annotation { "Feature Type Name" : "Feature", "Feature Type Description" : "" }
export const myFeature = defineFeature(function(context is Context, id is Id, definition is map)
    precondition{}
    {
        {
            var Q0;
            Q0=qCreatedBy(makeId("Front.planeOp"),FACE);
            var sketch = newSketch(context, id + "F0", { "sketchPlane" : qUnion([Q0])});
            skText(sketch, "E0", { "text": "Google ", "fontName": "NotoSansCJKtc-Bold.otf"});
            skLineSegment(sketch, "E1.bottom", {"start": v(5.86, 58.25) * mm, "end": v(124.9, 58.25) * mm});
            skLineSegment(sketch, "E1.top", {"start": v(5.86, -38.52) * mm, "end": v(124.9, -38.52) * mm});
            skLineSegment(sketch, "E1.left", {"start": v(5.86, 58.25) * mm, "end": v(5.86, -38.52) * mm});
            skLineSegment(sketch, "E1.right", {"start": v(124.9, 58.25) * mm, "end": v(124.9, -38.52) * mm});
            skLineSegment(sketch, "E2.bottom", {"start": v(0, 64.67) * mm, "end": v(130.03, 64.67) * mm});
            skLineSegment(sketch, "E2.top", {"start": v(0, -45.8) * mm, "end": v(130.03, -45.8) * mm});
            skLineSegment(sketch, "E2.left", {"start": v(0, 64.67) * mm, "end": v(0, -45.8) * mm});
            skLineSegment(sketch, "E2.right", {"start": v(130.03, 64.67) * mm, "end": v(130.03, -45.8) * mm});
            skLineSegment(sketch, "E3", {"start": v(-31.3, 35.82) * mm, "end": v(-31.3, 32.7) * mm});
            skLineSegment(sketch, "E4", {"start": v(-33.53, 35.16) * mm, "end": v(-33.53, 30.4) * mm});
            skLineSegment(sketch, "E5", {"start": v(-33.53, 30.4) * mm, "end": v(-29.58, 30.4) * mm});
            skLineSegment(sketch, "E6", {"start": v(-29.58, 30.4) * mm, "end": v(-27.53, 28.91) * mm});
            skLineSegment(sketch, "E7", {"start": v(-27.53, 28.91) * mm, "end": v(-27.53, 21.1) * mm});
            skLineSegment(sketch, "E8", {"start": v(-27.53, 21.1) * mm, "end": v(-29.42, 21.1) * mm});
            skLineSegment(sketch, "E9", {"start": v(-29.42, 21.1) * mm, "end": v(-31.15, 19.94) * mm});
            skLineSegment(sketch, "E10", {"start": v(-31.15, 19.94) * mm, "end": v(-25.47, 19.94) * mm});
            skLineSegment(sketch, "E11", {"start": v(-25.47, 19.94) * mm, "end": v(-25.47, 25.54) * mm});
            skLineSegment(sketch, "E12", {"start": v(-25.47, 25.54) * mm, "end": v(-22.5, 25.54) * mm});
            skLineSegment(sketch, "E13", {"start": v(-22.5, 25.54) * mm, "end": v(-22.5, 19.94) * mm});
            skLineSegment(sketch, "E14", {"start": v(-22.5, 19.94) * mm, "end": v(-18.64, 19.94) * mm});
            skLineSegment(sketch, "E15", {"start": v(-18.64, 19.94) * mm, "end": v(-19.4, 21.1) * mm});
            skLineSegment(sketch, "E16", {"start": v(-19.4, 21.1) * mm, "end": v(-20.86, 21.1) * mm});
            skLineSegment(sketch, "E17", {"start": v(-20.86, 21.1) * mm, "end": v(-20.86, 25.54) * mm});
            skLineSegment(sketch, "E18", {"start": v(-20.86, 25.54) * mm, "end": v(-20.86, 28.5) * mm});
            skLineSegment(sketch, "E19", {"start": v(-20.86, 28.5) * mm, "end": v(-18.9, 29.8) * mm});
            skLineSegment(sketch, "E20", {"start": v(-16.34, 29.8) * mm, "end": v(-18.9, 29.8) * mm});
            skLineSegment(sketch, "E21", {"start": v(-16.34, 29.8) * mm, "end": v(-16.34, 35) * mm});
            skLineSegment(sketch, "E22", {"start": v(-18.56, 35.82) * mm, "end": v(-18.56, 32.61) * mm});
            skLineSegment(sketch, "E23", {"start": v(-18.56, 32.61) * mm, "end": v(-21.27, 32.61) * mm});
            skLineSegment(sketch, "E24", {"start": v(-31.3, 32.7) * mm, "end": v(-26.84, 32.7) * mm});
            skLineSegment(sketch, "E25", {"start": v(-26.84, 32.7) * mm, "end": v(-26.84, 34.08) * mm});
            skLineSegment(sketch, "E26", {"start": v(-21.27, 32.61) * mm, "end": v(-21.27, 34.08) * mm});
            skArc(sketch, "E27", {"start": v(-24.99, 36.16) * mm, "mid": v(-26.31, 35.47) * mm, "end": v(-26.84, 34.08) * mm});
            skArc(sketch, "E28", {"start": v(-21.27, 34.08) * mm, "mid": v(-22.7, 35.9) * mm, "end": v(-24.99, 36.16) * mm});
            skArc(sketch, "E29", {"start": v(-26.84, 34.08) * mm, "mid": v(-26.64, 32.2) * mm, "end": v(-24.99, 31.3) * mm});
            skArc(sketch, "E30", {"start": v(-24.99, 31.3) * mm, "mid": v(-22.43, 31.76) * mm, "end": v(-21.27, 34.08) * mm});
            skLineSegment(sketch, "E31.bottom", {"start": v(150.76, 67.7) * mm, "end": v(295.17, 67.7) * mm});
            skLineSegment(sketch, "E31.top", {"start": v(150.76, -35.75) * mm, "end": v(295.17, -35.75) * mm});
            skLineSegment(sketch, "E31.left", {"start": v(150.76, 67.7) * mm, "end": v(150.76, -35.75) * mm});
            skLineSegment(sketch, "E31.right", {"start": v(295.17, 67.7) * mm, "end": v(295.17, -35.75) * mm});
            skPoint(sketch, "E32.oppositeSnap0", {"position": v(222.96, 67.7) * mm});
            skLineSegment(sketch, "E32.bottom", {"start": v(222.96, 67.7) * mm, "end": v(222.96, 67.7) * mm});
            skLineSegment(sketch, "E32.top", {"start": v(222.96, 106.62) * mm, "end": v(222.96, 106.62) * mm});
            skLineSegment(sketch, "E32.left", {"start": v(222.96, 67.7) * mm, "end": v(222.96, 106.62) * mm});
            skLineSegment(sketch, "E32.right", {"start": v(222.96, 67.7) * mm, "end": v(222.96, 106.62) * mm});
            skLineSegment(sketch, "E33", {"start": v(150.76, 67.7) * mm, "end": v(222.96, 106.62) * mm});
            skLineSegment(sketch, "E34", {"start": v(295.17, 67.7) * mm, "end": v(222.96, 106.62) * mm});
            const initialGuessF0  = {"E0": [-0.06541, -0.02444, 1, 0, 0.07026]};
            skSetInitialGuess(sketch, initialGuessF0);
            skSolve(sketch);
        }
        {
            var Q0;
            Q0=makeQuery(id+"F0.imprint","IMPRINT",FACE,{"disambiguationData":[TD([[makeQuery(id+"F0.imprint","IMPRINT",EDGE,{"derivedFrom":sQuery(id+"F0.wireOp",EDGE,"E0.sketch_text.stroke-0")}),1.0]])]});
            var Q1;
            Q1=makeQuery(id+"F0.imprint","IMPRINT",FACE,{"disambiguationData":[TD([[makeQuery(id+"F0.imprint","IMPRINT",EDGE,{"derivedFrom":sQuery(id+"F0.wireOp",EDGE,"E0.sketch_text.stroke-14")}),1.0]])]});
            var Q2;
            Q2=makeQuery(id+"F0.imprint","IMPRINT",FACE,{"disambiguationData":[TD([[makeQuery(id+"F0.imprint","IMPRINT",EDGE,{"derivedFrom":sQuery(id+"F0.wireOp",EDGE,"E0.sketch_text.stroke-22")}),1.0]])]});
            var Q3;
            Q3=makeQuery(id+"F0.imprint","IMPRINT",FACE,{"disambiguationData":[TD([[makeQuery(id+"F0.imprint","IMPRINT",EDGE,{"derivedFrom":sQuery(id+"F0.wireOp",EDGE,"E0.sketch_text.stroke-30")}),1.0]])]});
            var Q4;
            Q4=makeQuery(id+"F0.imprint","IMPRINT",FACE,{"disambiguationData":[TD([[makeQuery(id+"F0.imprint","IMPRINT",EDGE,{"derivedFrom":sQuery(id+"F0.wireOp",EDGE,"E0.sketch_text.stroke-60")}),1.0]])]});
            var Q5;
            Q5=makeQuery(id+"F0.imprint","IMPRINT",FACE,{"disambiguationData":[TD([[makeQuery(id+"F0.imprint","IMPRINT",EDGE,{"derivedFrom":sQuery(id+"F0.wireOp",EDGE,"E0.sketch_text.stroke-68")}),1.0]])]});
            extrude(context, id + "F1", {"entities" : qUnion([Q0, Q1, Q2, Q3, Q4, Q5]), "depth" : 25 * mm, "offsetDistance" : 25 * mm});
        }
        {
            var Q0;
            Q0=makeQuery(id+"F0.imprint","IMPRINT",FACE,{"disambiguationData":[TD([[makeQuery(id+"F0.imprint","IMPRINT",EDGE,{"derivedFrom":sQuery(id+"F0.wireOp",EDGE,"E1.bottom")}),1.0]])]});
            extrude(context, id + "F2", {"entities" : qUnion([Q0]), "depth" : 2.5 * mm, "offsetDistance" : 25 * mm});
        }
        {
            var Q0;
            Q0=makeQuery(id+"F0.imprint","IMPRINT",FACE,{"disambiguationData":[TD([[makeQuery(id+"F0.imprint","IMPRINT",EDGE,{"derivedFrom":sQuery(id+"F0.wireOp",EDGE,"E0.sketch_text.stroke-14")}),-1.0]])]});
            extrude(context, id + "F3", {"entities" : qUnion([Q0]), "depth" : 1 * mm, "offsetDistance" : 25 * mm});
        }
        {
            var Q0;
            Q0=makeQuery(id+"F3.opExtrude","CAP_FACE",FACE,{"disambiguationData":[OSD([sQuery(id+"F0.wireOp",EDGE,"E0.sketch_text.stroke-14"),sQuery(id+"F0.wireOp",EDGE,"E0.sketch_text.stroke-15"),sQuery(id+"F0.wireOp",EDGE,"E0.sketch_text.stroke-16"),sQuery(id+"F0.wireOp",EDGE,"E0.sketch_text.stroke-17"),sQuery(id+"F0.wireOp",EDGE,"E0.sketch_text.stroke-22"),sQuery(id+"F0.wireOp",EDGE,"E0.sketch_text.stroke-23"),sQuery(id+"F0.wireOp",EDGE,"E0.sketch_text.stroke-24"),sQuery(id+"F0.wireOp",EDGE,"E0.sketch_text.stroke-25"),sQuery(id+"F0.wireOp",EDGE,"E1.bottom"),sQuery(id+"F0.wireOp",EDGE,"E1.top"),sQuery(id+"F0.wireOp",EDGE,"E1.left"),sQuery(id+"F0.wireOp",EDGE,"E1.right")])],"isStart":false});
            var sketch = newSketch(context, id + "F4", { "sketchPlane" : qUnion([Q0])});
            skText(sketch, "E35", { "text": "Edukasja", "fontName": "OpenSans-Bold.ttf"});
            skText(sketch, "E36", { "text": "Ausbildung", "fontName": "OpenSans-Bold.ttf"});
            skText(sketch, "E37", { "text": "Education", "fontName": "OpenSans-Bold.ttf"});
            skText(sketch, "E38", { "text": "Svietnas", "fontName": "OpenSans-Regular.ttf"});
            skText(sketch, "E39", { "text": "Educasim", "fontName": "OpenSans-Regular.ttf"});
            const initialGuessF4  = {"E35": [0.0131, 0.05001, 1, 0, 0.0053], "E36": [0.06463, 0.04333, 1, 0, 0.00669], "E37": [0.03588, 0.0381, 0.96593, -0.25882, 0.00613], "E38": [0.07327, -0.03612, 1, 0, 0.00935], "E39": [0.0169, -0.03634, 1, 0, 0.00632]};
            skSetInitialGuess(sketch, initialGuessF4);
            skSolve(sketch);
        }
        {
            var Q0;
            Q0 = qSketchRegion(id + "F4", true);
            extrude(context, id + "F5", {"entities" : qUnion([Q0]), "operationType" : NewBodyOperationType.ADD, "depth" : 1.1 * mm, "offsetDistance" : 25 * mm});
        }
        {
            var Q0;
            {var subQ12=sQuery(id+"F0.wireOp",EDGE,"E5");Q0=makeQuery(id+"F0.imprint","IMPRINT",FACE,{"disambiguationData":[TD([[makeQuery(id+"F0.imprint","IMPRINT",EDGE,{"derivedFrom":subQ12}),1.0]])]});}
            var Q1;
            {var subQ0=sQuery(id+"F0.wireOp",EDGE,"E25");Q1=makeQuery(id+"F0.imprint","IMPRINT",FACE,{"disambiguationData":[TD([[makeQuery(id+"F0.imprint","IMPRINT",EDGE,{"derivedFrom":subQ0}),-1.0]])]});}
            extrude(context, id + "F6", {"entities" : qUnion([Q0, Q1]), "operationType" : NewBodyOperationType.ADD, "depth" : 15 * mm, "offsetDistance" : 25 * mm});
        }
        {
            var Q0;
            {var subQ2=sQuery(id+"F0.wireOp",EDGE,"E32.right");Q0=makeQuery(id+"F0.imprint","IMPRINT",FACE,{"disambiguationData":[TD([[makeQuery(id+"F0.imprint","IMPRINT",EDGE,{"derivedFrom":subQ2}),1.0]])]});}
            var Q1;
            {var subQ2=sQuery(id+"F0.wireOp",EDGE,"E32.right");Q1=makeQuery(id+"F0.imprint","IMPRINT",FACE,{"disambiguationData":[TD([[makeQuery(id+"F0.imprint","IMPRINT",EDGE,{"derivedFrom":subQ2}),-1.0]])]});}
            var Q2;
            {var subQ10=sQuery(id+"F0.wireOp",EDGE,"E0.sketch_text.stroke-31");Q2=makeQuery(id+"F0.imprint","IMPRINT",FACE,{"disambiguationData":[TD([[makeQuery(id+"F0.imprint","IMPRINT",EDGE,{"derivedFrom":subQ10}),-1.0]])]});}
            extrude(context, id + "F7", {"entities" : qUnion([Q0, Q1, Q2]), "depth" : 2.5 * mm, "offsetDistance" : 25 * mm});
        }
        {
            var Q0;
            {var subQ8=sQuery(id+"F0.wireOp",EDGE,"E0.sketch_text.stroke-34");Q0=makeQuery(id+"F0.imprint","IMPRINT",FACE,{"disambiguationData":[TD([[makeQuery(id+"F0.imprint","IMPRINT",EDGE,{"derivedFrom":subQ8}),1.0]])]});}
            var Q1;
            {var subQ12=sQuery(id+"F0.wireOp",EDGE,"E0.sketch_text.stroke-36");Q1=makeQuery(id+"F0.imprint","IMPRINT",FACE,{"disambiguationData":[TD([[makeQuery(id+"F0.imprint","IMPRINT",EDGE,{"derivedFrom":subQ12}),1.0]])]});}
            extrude(context, id + "F8", {"entities" : qUnion([Q0, Q1]), "depth" : 25 * mm, "offsetDistance" : 25 * mm});
        }
        {
            var Q0;
            Q0=makeQuery(id+"F7.opExtrude","CAP_FACE",FACE,{"disambiguationData":[OSD([sQuery(id+"F0.wireOp",EDGE,"E0.sketch_text.stroke-30"),sQuery(id+"F0.wireOp",EDGE,"E0.sketch_text.stroke-31"),sQuery(id+"F0.wireOp",EDGE,"E0.sketch_text.stroke-32"),sQuery(id+"F0.wireOp",EDGE,"E0.sketch_text.stroke-33"),sQuery(id+"F0.wireOp",EDGE,"E0.sketch_text.stroke-35"),sQuery(id+"F0.wireOp",EDGE,"E0.sketch_text.stroke-36"),sQuery(id+"F0.wireOp",EDGE,"E0.sketch_text.stroke-37"),sQuery(id+"F0.wireOp",EDGE,"E0.sketch_text.stroke-38"),sQuery(id+"F0.wireOp",EDGE,"E0.sketch_text.stroke-39"),sQuery(id+"F0.wireOp",EDGE,"E0.sketch_text.stroke-40"),sQuery(id+"F0.wireOp",EDGE,"E0.sketch_text.stroke-41"),sQuery(id+"F0.wireOp",EDGE,"E0.sketch_text.stroke-42"),sQuery(id+"F0.wireOp",EDGE,"E0.sketch_text.stroke-60"),sQuery(id+"F0.wireOp",EDGE,"E0.sketch_text.stroke-61"),sQuery(id+"F0.wireOp",EDGE,"E0.sketch_text.stroke-62"),sQuery(id+"F0.wireOp",EDGE,"E0.sketch_text.stroke-63"),sQuery(id+"F0.wireOp",EDGE,"E0.sketch_text.stroke-64"),sQuery(id+"F0.wireOp",EDGE,"E0.sketch_text.stroke-65"),sQuery(id+"F0.wireOp",EDGE,"E0.sketch_text.stroke-66"),sQuery(id+"F0.wireOp",EDGE,"E0.sketch_text.stroke-67"),sQuery(id+"F0.wireOp",EDGE,"E0.sketch_text.stroke-68"),sQuery(id+"F0.wireOp",EDGE,"E0.sketch_text.stroke-69"),sQuery(id+"F0.wireOp",EDGE,"E0.sketch_text.stroke-70"),sQuery(id+"F0.wireOp",EDGE,"E0.sketch_text.stroke-71"),sQuery(id+"F0.wireOp",EDGE,"E0.sketch_text.stroke-72"),sQuery(id+"F0.wireOp",EDGE,"E0.sketch_text.stroke-73"),sQuery(id+"F0.wireOp",EDGE,"E0.sketch_text.stroke-74"),sQuery(id+"F0.wireOp",EDGE,"E0.sketch_text.stroke-75"),sQuery(id+"F0.wireOp",EDGE,"E0.sketch_text.stroke-76"),sQuery(id+"F0.wireOp",EDGE,"E31.top"),sQuery(id+"F0.wireOp",EDGE,"E31.left"),sQuery(id+"F0.wireOp",EDGE,"E31.right"),sQuery(id+"F0.wireOp",EDGE,"E33"),sQuery(id+"F0.wireOp",EDGE,"E34")])],"isStart":false});
            var sketch = newSketch(context, id + "F9", { "sketchPlane" : qUnion([Q0])});
            skPoint(sketch, "E40.firstSnap0", {"position": v(186.86, 87.16) * mm});
            skText(sketch, "E41", { "text": "Sport Facility\n", "fontName": "OpenSans-Regular.ttf"});
            const initialGuessF9  = {"E41": [0.18162, 0.0634, 1, 0, 0.01163]};
            skSetInitialGuess(sketch, initialGuessF9);
            skSolve(sketch);
        }
        {
            var Q0;
            Q0=makeQuery(id+"F9.imprint","IMPRINT",FACE,{"disambiguationData":[TD([[makeQuery(id+"F9.imprint","IMPRINT",EDGE,{"derivedFrom":sQuery(id+"F9.wireOp",EDGE,"E41.sketch_text.stroke-0")}),-1.0]])]});
            var Q1;
            Q1=makeQuery(id+"F9.imprint","IMPRINT",FACE,{"disambiguationData":[TD([[makeQuery(id+"F9.imprint","IMPRINT",EDGE,{"derivedFrom":sQuery(id+"F9.wireOp",EDGE,"E41.sketch_text.stroke-25")}),-1.0]])]});
            var Q2;
            Q2=makeQuery(id+"F9.imprint","IMPRINT",FACE,{"disambiguationData":[TD([[makeQuery(id+"F9.imprint","IMPRINT",EDGE,{"derivedFrom":sQuery(id+"F9.wireOp",EDGE,"E41.sketch_text.stroke-50")}),-1.0]])]});
            var Q3;
            Q3=makeQuery(id+"F9.imprint","IMPRINT",FACE,{"disambiguationData":[TD([[makeQuery(id+"F9.imprint","IMPRINT",EDGE,{"derivedFrom":sQuery(id+"F9.wireOp",EDGE,"E41.sketch_text.stroke-67")}),-1.0]])]});
            var Q4;
            Q4=makeQuery(id+"F9.imprint","IMPRINT",FACE,{"disambiguationData":[TD([[makeQuery(id+"F9.imprint","IMPRINT",EDGE,{"derivedFrom":sQuery(id+"F9.wireOp",EDGE,"E41.sketch_text.stroke-80")}),-1.0]])]});
            var Q5;
            Q5=makeQuery(id+"F9.imprint","IMPRINT",FACE,{"disambiguationData":[TD([[makeQuery(id+"F9.imprint","IMPRINT",EDGE,{"derivedFrom":sQuery(id+"F9.wireOp",EDGE,"E41.sketch_text.stroke-99")}),-1.0]])]});
            var Q6;
            Q6=makeQuery(id+"F9.imprint","IMPRINT",FACE,{"disambiguationData":[TD([[makeQuery(id+"F9.imprint","IMPRINT",EDGE,{"derivedFrom":sQuery(id+"F9.wireOp",EDGE,"E41.sketch_text.stroke-109")}),-1.0]])]});
            var Q7;
            Q7=makeQuery(id+"F9.imprint","IMPRINT",FACE,{"disambiguationData":[TD([[makeQuery(id+"F9.imprint","IMPRINT",EDGE,{"derivedFrom":sQuery(id+"F9.wireOp",EDGE,"E41.sketch_text.stroke-136")}),-1.0]])]});
            var Q8;
            Q8=makeQuery(id+"F9.imprint","IMPRINT",FACE,{"disambiguationData":[TD([[makeQuery(id+"F9.imprint","IMPRINT",EDGE,{"derivedFrom":sQuery(id+"F9.wireOp",EDGE,"E41.sketch_text.stroke-151")}),-1.0]])]});
            var Q9;
            Q9=makeQuery(id+"F9.imprint","IMPRINT",FACE,{"disambiguationData":[TD([[makeQuery(id+"F9.imprint","IMPRINT",EDGE,{"derivedFrom":sQuery(id+"F9.wireOp",EDGE,"E41.sketch_text.stroke-163")}),-1.0]])]});
            var Q10;
            Q10=makeQuery(id+"F9.imprint","IMPRINT",FACE,{"disambiguationData":[TD([[makeQuery(id+"F9.imprint","IMPRINT",EDGE,{"derivedFrom":sQuery(id+"F9.wireOp",EDGE,"E41.sketch_text.stroke-167")}),-1.0]])]});
            var Q11;
            Q11=makeQuery(id+"F9.imprint","IMPRINT",FACE,{"disambiguationData":[TD([[makeQuery(id+"F9.imprint","IMPRINT",EDGE,{"derivedFrom":sQuery(id+"F9.wireOp",EDGE,"E41.sketch_text.stroke-171")}),-1.0]])]});
            var Q12;
            Q12=makeQuery(id+"F9.imprint","IMPRINT",FACE,{"disambiguationData":[TD([[makeQuery(id+"F9.imprint","IMPRINT",EDGE,{"derivedFrom":sQuery(id+"F9.wireOp",EDGE,"E41.sketch_text.stroke-155")}),-1.0]])]});
            var Q13;
            Q13=makeQuery(id+"F9.imprint","IMPRINT",FACE,{"disambiguationData":[TD([[makeQuery(id+"F9.imprint","IMPRINT",EDGE,{"derivedFrom":sQuery(id+"F9.wireOp",EDGE,"E41.sketch_text.stroke-179")}),-1.0]])]});
            var Q14;
            Q14=makeQuery(id+"F9.imprint","IMPRINT",FACE,{"disambiguationData":[TD([[makeQuery(id+"F9.imprint","IMPRINT",EDGE,{"derivedFrom":sQuery(id+"F9.wireOp",EDGE,"E41.sketch_text.stroke-198")}),-1.0]])]});
            extrude(context, id + "F10", {"entities" : qUnion([Q0, Q1, Q2, Q3, Q4, Q5, Q6, Q7, Q8, Q9, Q10, Q11, Q12, Q13, Q14]), "operationType" : NewBodyOperationType.ADD, "depth" : 1 * mm, "offsetDistance" : 25 * mm});
        }
        {
            var Q0;
            {var subQ0=sQuery(id+"F0.wireOp",EDGE,"E34");var subQ1=sQuery(id+"F0.wireOp",EDGE,"E33");var subQ2=sQuery(id+"F0.wireOp",EDGE,"E31.right");var subQ3=sQuery(id+"F0.wireOp",EDGE,"E31.left");var subQ4=sQuery(id+"F0.wireOp",EDGE,"E0.sketch_text.stroke-33");var subQ5=sQuery(id+"F0.wireOp",EDGE,"E0.sketch_text.stroke-35");var subQ6=sQuery(id+"F0.wireOp",EDGE,"E0.sketch_text.stroke-42");var subQ7=sQuery(id+"F0.wireOp",EDGE,"E31.top");var subQ8=sQuery(id+"F0.wireOp",EDGE,"E0.sketch_text.stroke-76");var subQ9=sQuery(id+"F0.wireOp",EDGE,"E0.sketch_text.stroke-75");var subQ10=sQuery(id+"F0.wireOp",EDGE,"E0.sketch_text.stroke-74");var subQ11=sQuery(id+"F0.wireOp",EDGE,"E0.sketch_text.stroke-73");var subQ12=sQuery(id+"F0.wireOp",EDGE,"E0.sketch_text.stroke-72");var subQ13=sQuery(id+"F0.wireOp",EDGE,"E0.sketch_text.stroke-71");var subQ14=sQuery(id+"F0.wireOp",EDGE,"E0.sketch_text.stroke-70");var subQ15=sQuery(id+"F0.wireOp",EDGE,"E0.sketch_text.stroke-69");var subQ16=sQuery(id+"F0.wireOp",EDGE,"E0.sketch_text.stroke-68");var subQ17=sQuery(id+"F0.wireOp",EDGE,"E0.sketch_text.stroke-67");var subQ18=sQuery(id+"F0.wireOp",EDGE,"E0.sketch_text.stroke-66");var subQ19=sQuery(id+"F0.wireOp",EDGE,"E0.sketch_text.stroke-63");var subQ20=sQuery(id+"F0.wireOp",EDGE,"E0.sketch_text.stroke-62");var subQ21=sQuery(id+"F0.wireOp",EDGE,"E0.sketch_text.stroke-61");var subQ22=sQuery(id+"F0.wireOp",EDGE,"E0.sketch_text.stroke-39");var subQ23=sQuery(id+"F0.wireOp",EDGE,"E0.sketch_text.stroke-41");var subQ24=sQuery(id+"F0.wireOp",EDGE,"E0.sketch_text.stroke-38");var subQ25=sQuery(id+"F0.wireOp",EDGE,"E0.sketch_text.stroke-40");var subQ26=sQuery(id+"F0.wireOp",EDGE,"E0.sketch_text.stroke-37");var subQ27=sQuery(id+"F0.wireOp",EDGE,"E0.sketch_text.stroke-36");var subQ28=sQuery(id+"F0.wireOp",EDGE,"E0.sketch_text.stroke-30");var subQ29=sQuery(id+"F0.wireOp",EDGE,"E0.sketch_text.stroke-31");var subQ30=sQuery(id+"F0.wireOp",EDGE,"E0.sketch_text.stroke-32");var subQ31=sQuery(id+"F0.wireOp",EDGE,"E0.sketch_text.stroke-60");var subQ32=sQuery(id+"F0.wireOp",EDGE,"E0.sketch_text.stroke-64");var subQ33=sQuery(id+"F0.wireOp",EDGE,"E0.sketch_text.stroke-65");Q0=makeQuery(id+"F10.boolean.opBoolean","SPLIT",FACE,{"disambiguationData":[TD([makeQuery(id+"F7.opExtrude","SWEPT_FACE",FACE,{"disambiguationData":[OSD([subQ28])]})])],"derivedFrom":makeQuery(id+"F7.opExtrude","CAP_FACE",FACE,{"disambiguationData":[OSD([subQ28,subQ29,subQ30,subQ4,subQ5,subQ27,subQ26,subQ24,subQ22,subQ25,subQ23,subQ6,subQ31,subQ21,subQ20,subQ19,subQ32,subQ33,subQ18,subQ17,subQ16,subQ15,subQ14,subQ13,subQ12,subQ11,subQ10,subQ9,subQ8,subQ7,subQ3,subQ2,subQ1,subQ0])],"isStart":false})});}
            var sketch = newSketch(context, id + "F11", { "sketchPlane" : qUnion([Q0])});
            skArc(sketch, "E42", {"start": v(265.82, 51.24) * mm, "mid": v(256.9, 55.6) * mm, "end": v(248.07, 51.03) * mm});
            skArc(sketch, "E43", {"start": v(248.07, 51.03) * mm, "mid": v(256.99, 47.4) * mm, "end": v(265.82, 51.24) * mm});
            skCircle(sketch, "E44", {"center": v(169.8, 54.42) * mm, "radius": 7.64 * mm});
            skLineSegment(sketch, "E45", {"start": v(169.8, 54.42) * mm, "end": v(177.43, 54.42) * mm});
            skLineSegment(sketch, "E46", {"start": v(169.8, 54.42) * mm, "end": v(169.8, 62.06) * mm});
            skLineSegment(sketch, "E47", {"start": v(169.8, 54.42) * mm, "end": v(169.8, 46.79) * mm});
            skLineSegment(sketch, "E48", {"start": v(169.8, 54.42) * mm, "end": v(162.16, 54.42) * mm});
            skLineSegment(sketch, "E49", {"start": v(165.98, 54.42) * mm, "end": v(165.98, 50.79) * mm});
            skLineSegment(sketch, "E50", {"start": v(165.98, 50.79) * mm, "end": v(169.8, 50.79) * mm});
            skLineSegment(sketch, "E51", {"start": v(169.8, 50.79) * mm, "end": v(173.9, 50.79) * mm});
            skLineSegment(sketch, "E52", {"start": v(173.9, 50.79) * mm, "end": v(173.9, 54.42) * mm});
            skLineSegment(sketch, "E53", {"start": v(173.9, 54.42) * mm, "end": v(173.9, 57.38) * mm});
            skLineSegment(sketch, "E54", {"start": v(173.9, 57.38) * mm, "end": v(169.8, 57.38) * mm});
            skLineSegment(sketch, "E55", {"start": v(169.8, 57.38) * mm, "end": v(167.01, 57.38) * mm});
            skLineSegment(sketch, "E56", {"start": v(165.98, 54.42) * mm, "end": v(165.98, 57.38) * mm});
            skLineSegment(sketch, "E57", {"start": v(173.9, 57.38) * mm, "end": v(173.9, 60.86) * mm});
            skLineSegment(sketch, "E58", {"start": v(173.9, 60.86) * mm, "end": v(173.9, 47.98) * mm});
            skLineSegment(sketch, "E59", {"start": v(173.9, 47.98) * mm, "end": v(165.98, 47.98) * mm});
            skLineSegment(sketch, "E60", {"start": v(165.98, 47.98) * mm, "end": v(165.98, 61.03) * mm});
            skLineSegment(sketch, "E61", {"start": v(165.98, 57.38) * mm, "end": v(167.01, 57.38) * mm});
            skLineSegment(sketch, "E62", {"start": v(173.9, 57.38) * mm, "end": v(176.83, 57.38) * mm});
            skLineSegment(sketch, "E63", {"start": v(173.9, 50.79) * mm, "end": v(176.51, 50.79) * mm});
            skLineSegment(sketch, "E64", {"start": v(165.98, 50.79) * mm, "end": v(163.08, 50.79) * mm});
            skLineSegment(sketch, "E65", {"start": v(165.98, 57.38) * mm, "end": v(162.76, 57.38) * mm});
            skCircle(sketch, "E66", {"center": v(222.78, 43.5) * mm, "radius": 4.45 * mm});
            skLineSegment(sketch, "E67.bottom", {"start": v(273.54, 18.71) * mm, "end": v(291.44, 18.71) * mm});
            skLineSegment(sketch, "E67.top", {"start": v(273.54, 5.89) * mm, "end": v(291.44, 5.89) * mm});
            skLineSegment(sketch, "E67.left", {"start": v(273.54, 18.71) * mm, "end": v(273.54, 5.89) * mm});
            skLineSegment(sketch, "E67.right", {"start": v(291.44, 18.71) * mm, "end": v(291.44, 5.89) * mm});
            skLineSegment(sketch, "E68", {"start": v(276.73, 5.89) * mm, "end": v(276.73, 12.64) * mm});
            skLineSegment(sketch, "E69", {"start": v(276.73, 12.64) * mm, "end": v(287.77, 12.64) * mm});
            skLineSegment(sketch, "E70", {"start": v(287.77, 12.64) * mm, "end": v(287.77, 5.89) * mm});
            skArc(sketch, "E71", {"start": v(276.73, 5.89) * mm, "mid": v(282.25, -0.98) * mm, "end": v(287.77, 5.89) * mm});
            skLineSegment(sketch, "E72", {"start": v(270.62, 31.67) * mm, "end": v(272.04, 30.25) * mm});
            skLineSegment(sketch, "E73", {"start": v(272.04, 30.25) * mm, "end": v(277.93, 34.72) * mm});
            skLineSegment(sketch, "E74", {"start": v(270.62, 31.67) * mm, "end": v(276.23, 35.93) * mm});
            skArc(sketch, "E75", {"start": v(279.66, 45.18) * mm, "mid": v(276.45, 41.1) * mm, "end": v(276.23, 35.93) * mm});
            skArc(sketch, "E76", {"start": v(285.95, 45.18) * mm, "mid": v(282.8, 46) * mm, "end": v(279.66, 45.18) * mm});
            skArc(sketch, "E77", {"start": v(287.88, 39.08) * mm, "mid": v(287.82, 42.42) * mm, "end": v(285.95, 45.18) * mm});
            skArc(sketch, "E78", {"start": v(277.93, 34.72) * mm, "mid": v(283.88, 34.67) * mm, "end": v(287.88, 39.08) * mm});
            skCircle(sketch, "E79", {"center": v(287.07, 32.08) * mm, "radius": 1.28 * mm});
            skLineSegment(sketch, "E80", {"start": v(274.33, -28.86) * mm, "end": v(279.32, -28.86) * mm});
            skLineSegment(sketch, "E81", {"start": v(274.33, -28.86) * mm, "end": v(276.63, -27.41) * mm});
            skLineSegment(sketch, "E82", {"start": v(276.63, -27.41) * mm, "end": v(278.07, -27.41) * mm});
            skLineSegment(sketch, "E83", {"start": v(278.07, -27.41) * mm, "end": v(278.07, -18.67) * mm});
            skLineSegment(sketch, "E84", {"start": v(279.32, -28.86) * mm, "end": v(279.32, -21.65) * mm});
            skLineSegment(sketch, "E85", {"start": v(279.32, -21.65) * mm, "end": v(281.82, -21.65) * mm});
            skLineSegment(sketch, "E86", {"start": v(281.82, -21.65) * mm, "end": v(281.82, -28.86) * mm});
            skLineSegment(sketch, "E87", {"start": v(281.82, -28.86) * mm, "end": v(286.82, -28.86) * mm});
            skLineSegment(sketch, "E88", {"start": v(286.82, -28.86) * mm, "end": v(285.47, -27.22) * mm});
            skLineSegment(sketch, "E89", {"start": v(285.47, -27.22) * mm, "end": v(283.93, -27.22) * mm});
            skLineSegment(sketch, "E90", {"start": v(283.93, -27.22) * mm, "end": v(283.93, -18.67) * mm});
            skLineSegment(sketch, "E91", {"start": v(278.07, -18.67) * mm, "end": v(278.07, -12.43) * mm});
            skLineSegment(sketch, "E92", {"start": v(278.07, -12.43) * mm, "end": v(275.77, -12.43) * mm});
            skLineSegment(sketch, "E93", {"start": v(275.77, -12.43) * mm, "end": v(273.27, -20.4) * mm});
            skLineSegment(sketch, "E94", {"start": v(273.27, -20.4) * mm, "end": v(271.39, -19.81) * mm});
            skLineSegment(sketch, "E95", {"start": v(271.39, -19.81) * mm, "end": v(274.64, -9.43) * mm});
            skLineSegment(sketch, "E96", {"start": v(274.64, -9.43) * mm, "end": v(279.32, -9.43) * mm});
            skLineSegment(sketch, "E97", {"start": v(283.93, -18.67) * mm, "end": v(283.93, -12.62) * mm});
            skLineSegment(sketch, "E98", {"start": v(283.93, -12.62) * mm, "end": v(286.14, -12.62) * mm});
            skLineSegment(sketch, "E99", {"start": v(286.14, -12.62) * mm, "end": v(287.78, -20.11) * mm});
            skLineSegment(sketch, "E100", {"start": v(287.78, -20.11) * mm, "end": v(289.99, -18.67) * mm});
            skLineSegment(sketch, "E101", {"start": v(289.99, -18.67) * mm, "end": v(287.78, -9.43) * mm});
            skLineSegment(sketch, "E102", {"start": v(287.78, -9.43) * mm, "end": v(282.97, -9.43) * mm});
            skLineSegment(sketch, "E103", {"start": v(282.97, -9.43) * mm, "end": v(282.97, -7.53) * mm});
            skLineSegment(sketch, "E104", {"start": v(279.32, -9.43) * mm, "end": v(279.32, -7.53) * mm});
            skArc(sketch, "E105", {"start": v(279.32, -3.3) * mm, "mid": v(278.5, -5.41) * mm, "end": v(279.32, -7.53) * mm});
            skArc(sketch, "E106", {"start": v(282.97, -2.82) * mm, "mid": v(281.05, -2.34) * mm, "end": v(279.32, -3.3) * mm});
            skArc(sketch, "E107", {"start": v(282.97, -7.53) * mm, "mid": v(284.19, -5.17) * mm, "end": v(282.97, -2.82) * mm});
            skArc(sketch, "E108", {"start": v(280.1, -6.18) * mm, "mid": v(281.25, -7.26) * mm, "end": v(282.5, -6.28) * mm});
            skCircle(sketch, "E109", {"center": v(280, -4.17) * mm, "radius": 0.58 * mm});
            skCircle(sketch, "E110", {"center": v(282.2, -4.36) * mm, "radius": 0.77 * mm});
            skLineSegment(sketch, "E111", {"start": v(280.1, -6.18) * mm, "end": v(282.5, -6.28) * mm});
            skSolve(sketch);
        }
        {
            var Q0;
            Q0=makeQuery(id+"F11.imprint","IMPRINT",FACE,{"disambiguationData":[TD([[makeQuery(id+"F11.imprint","IMPRINT",EDGE,{"derivedFrom":sQuery(id+"F11.wireOp",EDGE,"E42")}),1.0]])]});
            extrude(context, id + "F12", {"entities" : qUnion([Q0]), "depth" : 1 * mm, "offsetDistance" : 25 * mm});
        }
        {
            var Q0;
            {var subQ0=sQuery(id+"F11.wireOp",EDGE,"E50");Q0=makeQuery(id+"F11.imprint","IMPRINT",FACE,{"disambiguationData":[TD([[makeQuery(id+"F11.imprint","IMPRINT",EDGE,{"derivedFrom":subQ0}),-1.0]])]});}
            var Q1;
            {var subQ5=sQuery(id+"F11.wireOp",EDGE,"E51");Q1=makeQuery(id+"F11.imprint","IMPRINT",FACE,{"disambiguationData":[TD([[makeQuery(id+"F11.imprint","IMPRINT",EDGE,{"derivedFrom":subQ5}),1.0]])]});}
            var Q2;
            {var subQ4=sQuery(id+"F11.wireOp",EDGE,"E55");Q2=makeQuery(id+"F11.imprint","IMPRINT",FACE,{"disambiguationData":[TD([[makeQuery(id+"F11.imprint","IMPRINT",EDGE,{"derivedFrom":subQ4}),1.0]])]});}
            var Q3;
            {var subQ5=sQuery(id+"F11.wireOp",EDGE,"E54");Q3=makeQuery(id+"F11.imprint","IMPRINT",FACE,{"disambiguationData":[TD([[makeQuery(id+"F11.imprint","IMPRINT",EDGE,{"derivedFrom":subQ5}),-1.0]])]});}
            var Q4;
            {var subQ3=sQuery(id+"F11.wireOp",EDGE,"E65");Q4=makeQuery(id+"F11.imprint","IMPRINT",FACE,{"disambiguationData":[TD([[makeQuery(id+"F11.imprint","IMPRINT",EDGE,{"derivedFrom":subQ3}),-1.0]])]});}
            var Q5;
            {var subQ3=sQuery(id+"F11.wireOp",EDGE,"E64");Q5=makeQuery(id+"F11.imprint","IMPRINT",FACE,{"disambiguationData":[TD([[makeQuery(id+"F11.imprint","IMPRINT",EDGE,{"derivedFrom":subQ3}),-1.0]])]});}
            var Q6;
            {var subQ3=sQuery(id+"F11.wireOp",EDGE,"E62");Q6=makeQuery(id+"F11.imprint","IMPRINT",FACE,{"disambiguationData":[TD([[makeQuery(id+"F11.imprint","IMPRINT",EDGE,{"derivedFrom":subQ3}),-1.0]])]});}
            var Q7;
            {var subQ3=sQuery(id+"F11.wireOp",EDGE,"E63");Q7=makeQuery(id+"F11.imprint","IMPRINT",FACE,{"disambiguationData":[TD([[makeQuery(id+"F11.imprint","IMPRINT",EDGE,{"derivedFrom":subQ3}),-1.0]])]});}
            extrude(context, id + "F13", {"entities" : qUnion([Q0, Q1, Q2, Q3, Q4, Q5, Q6, Q7]), "depth" : 1 * mm, "offsetDistance" : 25 * mm});
        }
        {
            var Q0;
            Q0=makeQuery(id+"F13.opExtrude","SWEPT_BODY",BODY,{"disambiguationData":[OSD([sQuery(id+"F11.wireOp",EDGE,"E44"),sQuery(id+"F11.wireOp",EDGE,"E46"),sQuery(id+"F11.wireOp",EDGE,"E54"),sQuery(id+"F11.wireOp",EDGE,"E58")])]});
            var Q1;
            Q1=makeQuery(id+"F13.opExtrude","SWEPT_BODY",BODY,{"disambiguationData":[OSD([sQuery(id+"F11.wireOp",EDGE,"E44"),sQuery(id+"F11.wireOp",EDGE,"E58"),sQuery(id+"F11.wireOp",EDGE,"E63")])]});
            var Q2;
            Q2=makeQuery(id+"F13.opExtrude","SWEPT_BODY",BODY,{"disambiguationData":[OSD([sQuery(id+"F11.wireOp",EDGE,"E47"),sQuery(id+"F11.wireOp",EDGE,"E50"),sQuery(id+"F11.wireOp",EDGE,"E59"),sQuery(id+"F11.wireOp",EDGE,"E60")])]});
            var Q3;
            Q3=makeQuery(id+"F13.opExtrude","SWEPT_BODY",BODY,{"disambiguationData":[OSD([sQuery(id+"F11.wireOp",EDGE,"E45"),sQuery(id+"F11.wireOp",EDGE,"E47"),sQuery(id+"F11.wireOp",EDGE,"E51"),sQuery(id+"F11.wireOp",EDGE,"E58")])]});
            var Q4;
            Q4=makeQuery(id+"F13.opExtrude","SWEPT_BODY",BODY,{"disambiguationData":[OSD([sQuery(id+"F11.wireOp",EDGE,"E44"),sQuery(id+"F11.wireOp",EDGE,"E45"),sQuery(id+"F11.wireOp",EDGE,"E58"),sQuery(id+"F11.wireOp",EDGE,"E62")])]});
            var Q5;
            Q5=makeQuery(id+"F13.opExtrude","SWEPT_BODY",BODY,{"disambiguationData":[OSD([sQuery(id+"F11.wireOp",EDGE,"E44"),sQuery(id+"F11.wireOp",EDGE,"E60"),sQuery(id+"F11.wireOp",EDGE,"E65")])]});
            var Q6;
            Q6=makeQuery(id+"F13.opExtrude","SWEPT_BODY",BODY,{"disambiguationData":[OSD([sQuery(id+"F11.wireOp",EDGE,"E44"),sQuery(id+"F11.wireOp",EDGE,"E48"),sQuery(id+"F11.wireOp",EDGE,"E60"),sQuery(id+"F11.wireOp",EDGE,"E64")])]});
            var Q7;
            Q7=makeQuery(id+"F13.opExtrude","SWEPT_BODY",BODY,{"disambiguationData":[OSD([sQuery(id+"F11.wireOp",EDGE,"E46"),sQuery(id+"F11.wireOp",EDGE,"E48"),sQuery(id+"F11.wireOp",EDGE,"E55"),sQuery(id+"F11.wireOp",EDGE,"E60"),sQuery(id+"F11.wireOp",EDGE,"E61")])]});
            transform(context, id + "F14", {"entities" : qUnion([Q0, Q1, Q2, Q3, Q4, Q5, Q6, Q7]), "transformType" : TransformType.TRANSLATION_3D, "dx" : 0 * mm, "dy" : 0 * mm, "dz" : 12.6 * mm, "makeCopy" : false});
        }
        {
            var Q0;
            Q0=makeQuery(id+"F11.imprint","IMPRINT",FACE,{"disambiguationData":[TD([[makeQuery(id+"F11.imprint","IMPRINT",EDGE,{"derivedFrom":sQuery(id+"F11.wireOp",EDGE,"E67.bottom")}),-1.0]])]});
            extrude(context, id + "F15", {"entities" : qUnion([Q0]), "depth" : 2.5 * mm, "offsetDistance" : 25 * mm});
        }
        {
            var Q0;
            {var subQ1=sQuery(id+"F11.wireOp",EDGE,"E68");Q0=makeQuery(id+"F11.imprint","IMPRINT",FACE,{"disambiguationData":[TD([[makeQuery(id+"F11.imprint","IMPRINT",EDGE,{"derivedFrom":subQ1}),-1.0]])]});}
            extrude(context, id + "F16", {"entities" : qUnion([Q0]), "depth" : 1 * mm, "offsetDistance" : 25 * mm});
        }
        {
            var Q0;
            {var subQ0=sQuery(id+"F11.wireOp",EDGE,"E71");Q0=makeQuery(id+"F11.imprint","IMPRINT",FACE,{"disambiguationData":[TD([[makeQuery(id+"F11.imprint","IMPRINT",EDGE,{"derivedFrom":subQ0}),1.0]])]});}
            extrude(context, id + "F17", {"entities" : qUnion([Q0]), "depth" : 25 * mm, "offsetDistance" : 25 * mm});
        }
        {
            var Q0;
            Q0=makeQuery(id+"F17.opExtrude","SWEPT_FACE",FACE,{"disambiguationData":[OSD([sQuery(id+"F11.wireOp",EDGE,"E67.top")])]});
            var sketch = newSketch(context, id + "F18", { "sketchPlane" : qUnion([Q0])});
            skArc(sketch, "E112", {"start": v(276.73, -4.89) * mm, "mid": v(282.22, -10.26) * mm, "end": v(287.77, -4.95) * mm});
            skSolve(sketch);
        }
        {
            var Q0;
            {var subQ0=sQuery(id+"F18.wireOp",EDGE,"E112");Q0=makeQuery(id+"F18.imprint","IMPRINT",FACE,{"disambiguationData":[TD([[makeQuery(id+"F18.imprint","IMPRINT",EDGE,{"derivedFrom":subQ0}),1.0]])]});}
            extrude(context, id + "F19", {"entities" : qUnion([Q0]), "oppositeDirection" : true, "depth" : 7 * mm, "offsetDistance" : 25 * mm});
        }
        {
            var Q0;
            Q0=makeQuery(id+"F11.imprint","IMPRINT",FACE,{"disambiguationData":[TD([[makeQuery(id+"F11.imprint","IMPRINT",EDGE,{"derivedFrom":sQuery(id+"F11.wireOp",EDGE,"E72")}),1.0]])]});
            var Q1;
            Q1=makeQuery(id+"F11.imprint","IMPRINT",FACE,{"disambiguationData":[TD([[makeQuery(id+"F11.imprint","IMPRINT",EDGE,{"derivedFrom":sQuery(id+"F11.wireOp",EDGE,"E79")}),1.0]])]});
            extrude(context, id + "F20", {"entities" : qUnion([Q0, Q1]), "operationType" : NewBodyOperationType.ADD, "depth" : 1 * mm, "offsetDistance" : 25 * mm});
        }
        {
            var Q0;
            Q0=makeQuery(id+"F11.imprint","IMPRINT",FACE,{"disambiguationData":[TD([[makeQuery(id+"F11.imprint","IMPRINT",EDGE,{"derivedFrom":sQuery(id+"F11.wireOp",EDGE,"E66")}),1.0]])]});
            extrude(context, id + "F21", {"entities" : qUnion([Q0]), "depth" : 1 * mm, "offsetDistance" : 25 * mm});
        }
        {
            var Q0;
            Q0=makeQuery(id+"F19.opExtrude","SWEPT_BODY",BODY,{"disambiguationData":[OSD([sQuery(id+"F11.wireOp",EDGE,"E67.top"),sQuery(id+"F11.wireOp",EDGE,"E68"),sQuery(id+"F11.wireOp",EDGE,"E70"),sQuery(id+"F11.wireOp",EDGE,"E71"),sQuery(id+"F18.wireOp",EDGE,"E112")])]});
            transform(context, id + "F22", {"entities" : qUnion([Q0]), "transformType" : TransformType.TRANSLATION_3D, "dx" : -111.9 * mm, "dy" : 0 * mm, "dz" : 34 * mm, "makeCopy" : false});
        }
        {
            var Q0;
            Q0=makeQuery(id+"F15.opExtrude","SWEPT_BODY",BODY,{"disambiguationData":[OSD([sQuery(id+"F11.wireOp",EDGE,"E67.bottom"),sQuery(id+"F11.wireOp",EDGE,"E67.top"),sQuery(id+"F11.wireOp",EDGE,"E67.left"),sQuery(id+"F11.wireOp",EDGE,"E67.right"),sQuery(id+"F11.wireOp",EDGE,"E68"),sQuery(id+"F11.wireOp",EDGE,"E69"),sQuery(id+"F11.wireOp",EDGE,"E70")])]});
            transform(context, id + "F23", {"entities" : qUnion([Q0]), "transformType" : TransformType.TRANSLATION_3D, "dx" : -112.1 * mm, "dy" : 0 * mm, "dz" : 33 * mm, "makeCopy" : false});
        }
        {
            var Q0;
            Q0=makeQuery(id+"F16.opExtrude","SWEPT_BODY",BODY,{"disambiguationData":[OSD([sQuery(id+"F11.wireOp",EDGE,"E67.top"),sQuery(id+"F11.wireOp",EDGE,"E68"),sQuery(id+"F11.wireOp",EDGE,"E69"),sQuery(id+"F11.wireOp",EDGE,"E70")])]});
            transform(context, id + "F24", {"entities" : qUnion([Q0]), "transformType" : TransformType.TRANSLATION_3D, "dx" : -112.1 * mm, "dy" : 0 * mm, "dz" : 32.7 * mm, "makeCopy" : false});
        }
        {
            var Q0;
            Q0=makeQuery(id+"F11.imprint","IMPRINT",FACE,{"disambiguationData":[TD([[makeQuery(id+"F11.imprint","IMPRINT",EDGE,{"derivedFrom":sQuery(id+"F11.wireOp",EDGE,"E80")}),1.0]])]});
            extrude(context, id + "F25", {"entities" : qUnion([Q0]), "operationType" : NewBodyOperationType.ADD, "depth" : 1 * mm, "offsetDistance" : 25 * mm});
        }
        {
            var Q0;
            Q0=makeQuery(id+"F11.imprint","IMPRINT",FACE,{"disambiguationData":[TD([[makeQuery(id+"F11.imprint","IMPRINT",EDGE,{"derivedFrom":sQuery(id+"F11.wireOp",EDGE,"E108")}),1.0]])]});
            extrude(context, id + "F26", {"entities" : qUnion([Q0]), "operationType" : NewBodyOperationType.ADD, "depth" : 0.7 * mm, "offsetDistance" : 25 * mm});
        }
        {
            var Q0;
            Q0=makeQuery(id+"F25.opExtrude","CAP_EDGE",EDGE,{"disambiguationData":[OSD([sQuery(id+"F11.wireOp",EDGE,"E101")])],"isStart":false});
            var Q1;
            Q1=makeQuery(id+"F25.opExtrude","CAP_EDGE",EDGE,{"disambiguationData":[OSD([sQuery(id+"F11.wireOp",EDGE,"E99")])],"isStart":false});
            var Q2;
            Q2=makeQuery(id+"F25.opExtrude","CAP_EDGE",EDGE,{"disambiguationData":[OSD([sQuery(id+"F11.wireOp",EDGE,"E90"),sQuery(id+"F11.wireOp",EDGE,"E97")])],"isStart":false});
            var Q3;
            Q3=makeQuery(id+"F25.opExtrude","CAP_EDGE",EDGE,{"disambiguationData":[OSD([sQuery(id+"F11.wireOp",EDGE,"E93")])],"isStart":false});
            var Q4;
            Q4=makeQuery(id+"F25.opExtrude","CAP_EDGE",EDGE,{"disambiguationData":[OSD([sQuery(id+"F11.wireOp",EDGE,"E95")])],"isStart":false});
            var Q5;
            Q5=makeQuery(id+"F25.opExtrude","CAP_EDGE",EDGE,{"disambiguationData":[OSD([sQuery(id+"F11.wireOp",EDGE,"E92")])],"isStart":false});
            var Q6;
            Q6=makeQuery(id+"F25.opExtrude","CAP_EDGE",EDGE,{"disambiguationData":[OSD([sQuery(id+"F11.wireOp",EDGE,"E83"),sQuery(id+"F11.wireOp",EDGE,"E91")])],"isStart":false});
            var Q7;
            Q7=makeQuery(id+"F25.opExtrude","CAP_EDGE",EDGE,{"disambiguationData":[OSD([sQuery(id+"F11.wireOp",EDGE,"E85")])],"isStart":false});
            var Q8;
            Q8=makeQuery(id+"F25.opExtrude","CAP_EDGE",EDGE,{"disambiguationData":[OSD([sQuery(id+"F11.wireOp",EDGE,"E102")])],"isStart":false});
            var Q9;
            Q9=makeQuery(id+"F25.opExtrude","CAP_EDGE",EDGE,{"disambiguationData":[OSD([sQuery(id+"F11.wireOp",EDGE,"E96")])],"isStart":false});
            fillet(context, id + "F27", {"entities" : qUnion([Q0, Q1, Q2, Q3, Q4, Q5, Q6, Q7, Q8, Q9]), "radius" : 0.5 * mm, "tangentPropagation" : true, "allowEdgeOverflow" : false});
        }
    });